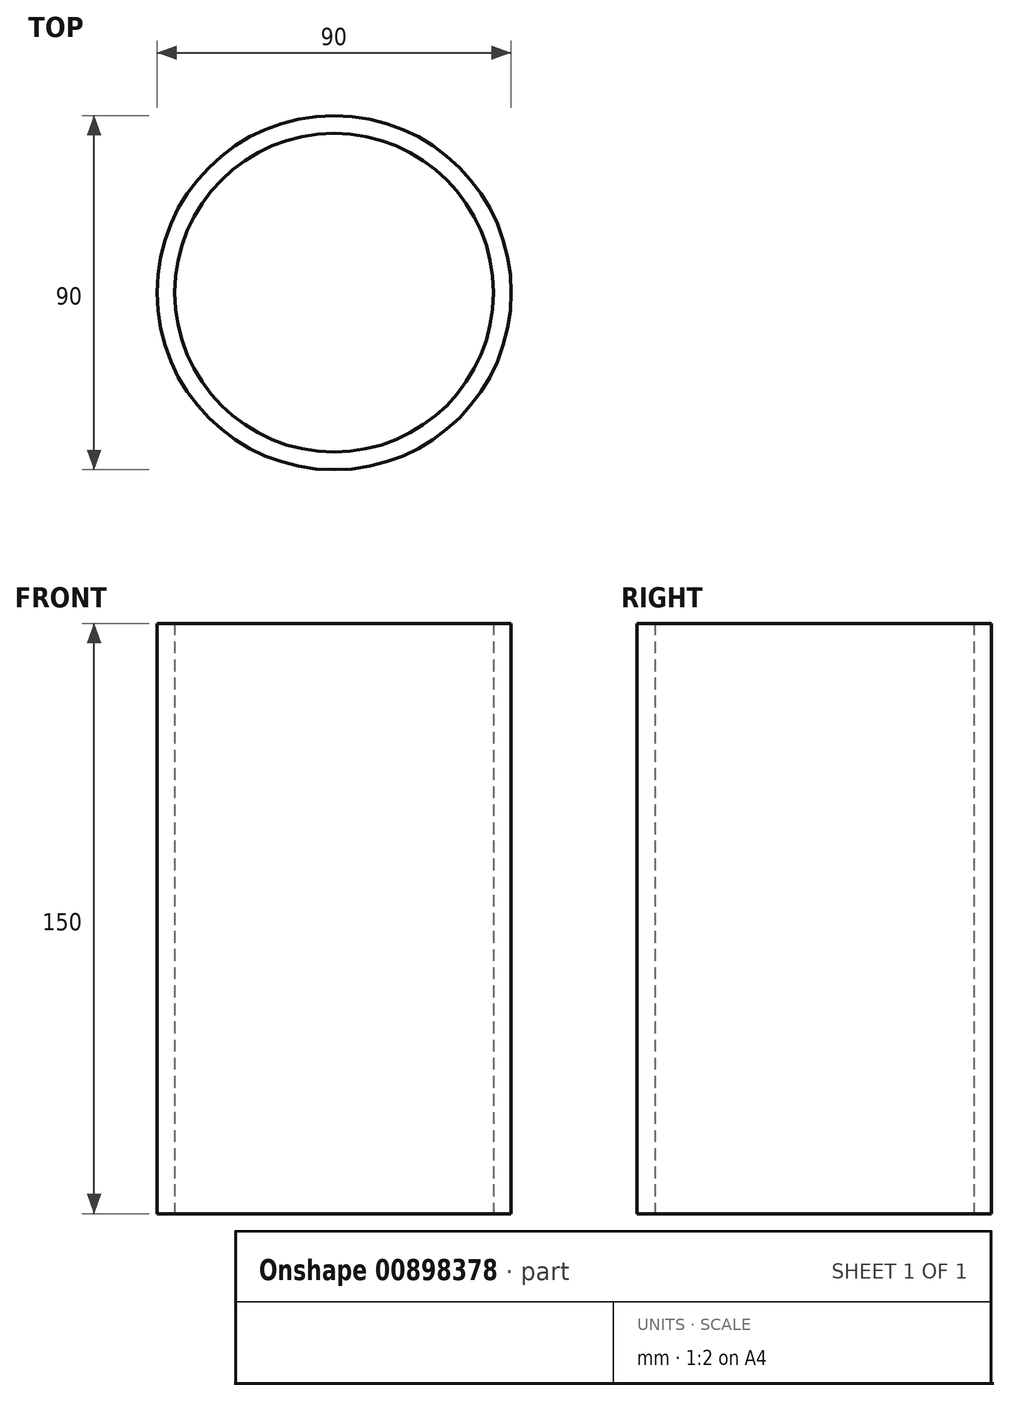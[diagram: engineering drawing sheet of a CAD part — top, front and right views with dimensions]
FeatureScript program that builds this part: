
annotation { "Feature Type Name" : "Feature", "Feature Type Description" : "" }
export const myFeature = defineFeature(function(context is Context, id is Id, definition is map)
    precondition{}
    {
        {
            var Q0;
            Q0=qCreatedBy(makeId("Top.planeOp"),FACE);
            var sketch = newSketch(context, id + "F0", { "sketchPlane" : qUnion([Q0])});
            skCircle(sketch, "E0", {"center": v(0, 0) * mm, "radius": 45 * mm});
            skCircle(sketch, "E1", {"center": v(0, 0) * mm, "radius": 40.5 * mm});
            skSolve(sketch);
        }
        {
            var Q0;
            Q0=makeQuery(id+"F0.imprint","IMPRINT",FACE,{"disambiguationData":[TD([[makeQuery(id+"F0.imprint","IMPRINT",EDGE,{"derivedFrom":sQuery(id+"F0.wireOp",EDGE,"E0")}),1.0]])]});
            extrude(context, id + "F1", {"entities" : qUnion([Q0]), "depth" : 150 * mm, "offsetDistance" : 25 * mm});
        }
    });
